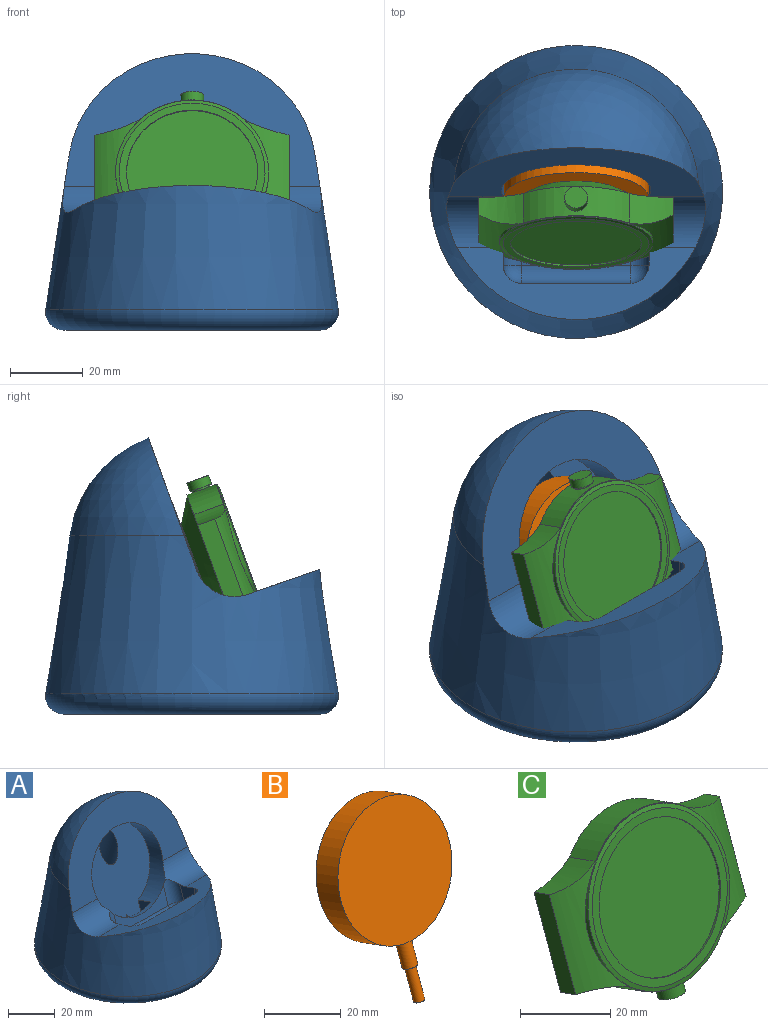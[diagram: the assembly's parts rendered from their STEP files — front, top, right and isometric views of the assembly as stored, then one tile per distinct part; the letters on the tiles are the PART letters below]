
ASSEMBLY  parts=3 mates=2
PART A: 40 faces, bbox 87.7x87.7x79.4 mm
  f0: plane 53.83x41.32mm, normal (0,-0.94,0.34), area 1416.9mm2, adj f1,f3,f10,f17,f18,f36,f37,f38
  f1: plane 26.33x14.1mm, normal (1,0,0), area 101.3mm2, adj f0,f5,f7,f36,f38,f39
  f2: plane 7.33x1.53mm, normal (1,0,0), area 9mm2, adj f6,f7,f8,f39
  f3: plane 26.33x14.1mm, normal (-1,0,0), area 101.3mm2, adj f0,f5,f7,f36,f37,f39
  f4: plane 7.33x1.53mm, normal (-1,0,0), area 9mm2, adj f6,f7,f8,f39
  f5: cylinder r=1.5mm len=8.77mm, axis (0,1,0), area 41.3mm2, adj f1,f3,f36,f39
  f6: cylinder r=1.5mm len=8.35mm, axis (0,1,0), area 36.9mm2, adj f2,f4,f8,f39
  f7: plane 70.73x70.7mm, normal (0,0,-1), area 3485.4mm2, adj f1,f2,f3,f4,f8,f16,f17,f18
  f8: torus R=35.19mm, axis (0,0,-1), area 2067.4mm2, adj f2,f4,f6,f7,f13
  f9: plane 66.13x20.56mm, normal (0,0.33,0.95), area 570.7mm2, adj f11,f12,f13,f20,f22,f23,f29,f32
  f10: cylinder r=20.5mm len=42.3mm, axis (0,-0.94,0.34), area 1066.8mm2, adj f0,f11,f12,f15,f16,f17,f18,f19
  f11: cylinder r=11.03mm len=18.2mm, axis (1,0,0), area 259.1mm2, adj f9,f10,f13,f15,f22,f24
  f12: cylinder r=11.03mm len=18.2mm, axis (1,0,0), area 259.1mm2, adj f9,f10,f13,f15,f23,f26
  f13: cone r=33.62mm half-angle=8.6deg, axis (0,0,-1), area 8751.7mm2, adj f8,f9,f11,f12,f14,f15
  f14: sphere r=34mm, area 2256.5mm2, adj f13,f15
  f15: plane 70.19x36.45mm, normal (0,-0.94,0.34), area 1291.6mm2, adj f10,f11,f12,f13,f14
  f16: plane 25.96x16mm, normal (0,0.94,-0.34), area 424.5mm2, adj f7,f10,f17,f18
  f17: plane 25.96x16.97mm, normal (1,0,0), area 221.1mm2, adj f0,f7,f10,f16,f38
  f18: plane 25.96x16.97mm, normal (-1,0,0), area 221.1mm2, adj f0,f7,f10,f16,f37
  f19: plane 30.12x8.91mm, normal (0,-0.95,0.33), area 143.6mm2, adj f10,f24,f25,f26
  f20: plane 30x11.94mm, normal (0,1,0), area 358.2mm2, adj f9,f29,f32,f35
  f21: plane 30x5.94mm, normal (0,0,1), area 178.2mm2, adj f25,f30,f31,f35
  f22: plane 10.21x8.67mm, normal (1,0,0), area 65.6mm2, adj f9,f11,f24,f29,f30
  f23: plane 10.21x8.67mm, normal (-1,0,0), area 65.6mm2, adj f9,f12,f26,f31,f32
  f24: cylinder r=5mm len=12.59mm, axis (0,0.33,0.95), area 79.2mm2, adj f10,f11,f19,f22,f27
  f25: cylinder r=5mm len=30mm, axis (-1,0,0), area 185.7mm2, adj f19,f21,f27,f28
  f26: cylinder r=5mm len=12.59mm, axis (0,-0.33,-0.95), area 79.2mm2, adj f10,f12,f19,f23,f28
  f27: sphere r=5mm, area 32.8mm2, adj f24,f25,f30
  f28: sphere r=5mm, area 32.8mm2, adj f25,f26,f31
  f29: cylinder r=5mm len=11.94mm, axis (0,0,-1), area 87mm2, adj f9,f20,f22,f33
  f30: cylinder r=5mm len=5.94mm, axis (0,1,0), area 46.6mm2, adj f21,f22,f27,f33
  f31: cylinder r=5mm len=5.94mm, axis (0,-1,0), area 46.6mm2, adj f21,f23,f28,f34
  f32: cylinder r=5mm len=11.94mm, axis (0,0,1), area 87mm2, adj f9,f20,f23,f34
  f33: sphere r=5mm, area 39.3mm2, adj f29,f30,f35
  f34: sphere r=5mm, area 39.3mm2, adj f31,f32,f35
  f35: cylinder r=5mm len=30mm, axis (-1,0,0), area 235.6mm2, adj f20,f21,f33,f34
  f36: torus R=14.22mm, axis (1,0,0), area 105.2mm2, adj f0,f1,f3,f5
  f37: cylinder r=5mm len=6.71mm, axis (1,0,0), area 62.4mm2, adj f0,f3,f7,f18
  f38: cylinder r=5mm len=6.71mm, axis (1,0,0), area 62.4mm2, adj f0,f1,f7,f17
  f39: cylinder r=5mm len=61.21mm, axis (0,0.29,-0.96), area 1638.9mm2, adj f0,f1,f2,f3,f4,f5,f6,f7
PART B: 7 faces, bbox 39.9x25.3x56.4 mm
  f0: cylinder r=19.93mm len=40.4mm, axis (0,-0.94,0.34), area 1062.7mm2, adj f1,f2,f3
  f1: plane 39.86x37.46mm, normal (0,0.94,-0.34), area 1247.9mm2, adj f0
  f2: plane 39.86x37.46mm, normal (0,-0.94,0.34), area 1247.9mm2, adj f0
  f3: cylinder r=2.12mm len=9.13mm, axis (0,0.34,0.94), area 108.3mm2, adj f0,f4
  f4: plane 4.25x3.99mm, normal (0,-0.34,-0.94), area 7.1mm2, adj f3,f5
  f5: cylinder r=1.5mm len=10.42mm, axis (0,0.34,0.94), area 94.2mm2, adj f4,f6
  f6: plane 3x2.82mm, normal (0,-0.34,-0.94), area 7.1mm2, adj f5
PART C: 26 faces, bbox 53.3x24.2x45 mm
  f0: plane 29.06x5.58mm, normal (0,-0.94,0.34), area 3.2mm2, adj f7,f11,f12,f13
  f1: plane 24.64x13.04mm, normal (-1,0,0), area 122mm2, adj f5,f6,f10,f12
  f2: plane 24.64x13.04mm, normal (1,0,0), area 122mm2, adj f8,f9,f10,f11
  f3: plane 29.06x5.58mm, normal (0,-0.94,0.34), area 3.2mm2, adj f4,f11,f12,f13
  f4: cylinder r=21.1mm len=29.06mm, axis (0,0.94,-0.34), area 275.7mm2, adj f3,f5,f9,f10
  f5: cylinder r=25.24mm len=12.12mm, axis (0,0.94,-0.34), area 94.5mm2, adj f1,f4,f10,f12
  f6: cylinder r=25.24mm len=12.12mm, axis (0,0.94,-0.34), area 94.5mm2, adj f1,f7,f10,f12
  f7: cylinder r=21.1mm len=29.06mm, axis (0,0.94,-0.34), area 256mm2, adj f0,f6,f8,f10,f22
  f8: cylinder r=25.24mm len=12.12mm, axis (0,0.94,-0.34), area 94.5mm2, adj f2,f7,f10,f11
  f9: cylinder r=25.24mm len=12.12mm, axis (0,0.94,-0.34), area 94.5mm2, adj f2,f4,f10,f11
  f10: plane 53.3x39.66mm, normal (0,0.94,-0.34), area 421.6mm2, adj f1,f2,f4,f5,f6,f7,f8,f9
  f11: cylinder r=22.2mm len=29.99mm, axis (0,0.34,0.94), area 200.8mm2, adj f0,f2,f3,f8,f9,f13
  f12: cylinder r=22.2mm len=29.99mm, axis (0,0.34,0.94), area 200.8mm2, adj f0,f1,f3,f5,f6,f13
  f13: cylinder r=21mm len=42mm, axis (0,0.94,-0.34), area 67.1mm2, adj f0,f3,f11,f12,f17
  f14: plane 40x37.59mm, normal (0,-0.94,0.34), area 238.8mm2, adj f15,f17
  f15: cylinder r=18mm len=36mm, axis (0,-0.94,0.34), area 56.5mm2, adj f14,f16
  f16: plane 36x33.83mm, normal (0,-0.94,0.34), area 1017.9mm2, adj f15
  f17: cone r=21mm half-angle=76deg, axis (0,0.94,-0.34), area 132.8mm2, adj f13,f14
  f18: plane 28x26.31mm, normal (0,0.94,-0.34), area 527.5mm2, adj f19,f21
  f19: cone r=20.65mm half-angle=58.1deg, axis (0,-0.94,0.34), area 852.7mm2, adj f10,f18
  f20: plane 10x9.4mm, normal (0,0.94,-0.34), area 78.5mm2, adj f21
  f21: cone r=5mm half-angle=45deg, axis (0,-0.94,0.34), area 13.7mm2, adj f18,f20
  f22: cylinder r=2.5mm len=5mm, axis (0,-0.34,-0.94), area 9mm2, adj f7,f25
  f23: cylinder r=3.15mm len=6.78mm, axis (0,0.34,0.94), area 49.5mm2, adj f24,f25
  f24: plane 6.3x5.92mm, normal (0,-0.34,-0.94), area 31.2mm2, adj f23
  f25: plane 6.3x5.92mm, normal (0,0.34,0.94), area 11.5mm2, adj f22,f23
PLACE A t=(-76.29,16.46,27.68)mm
PLACE B rot(axis=(0.15,0.95,0.27),0deg) t=(-76.29,14.61,22.58)mm
PLACE C rot(axis=(0,-0.94,0.34),180deg) t=(-76.29,42.89,100.28)mm
MATE fastened B.f0 <-> C.f21  axis (0,-0.94,0.34) through (-76.29,14.88,66.48)mm
MATE fastened A.f0 <-> B.f0  axis (0,-0.94,0.34) through (-76.29,22.96,63.54)mm
